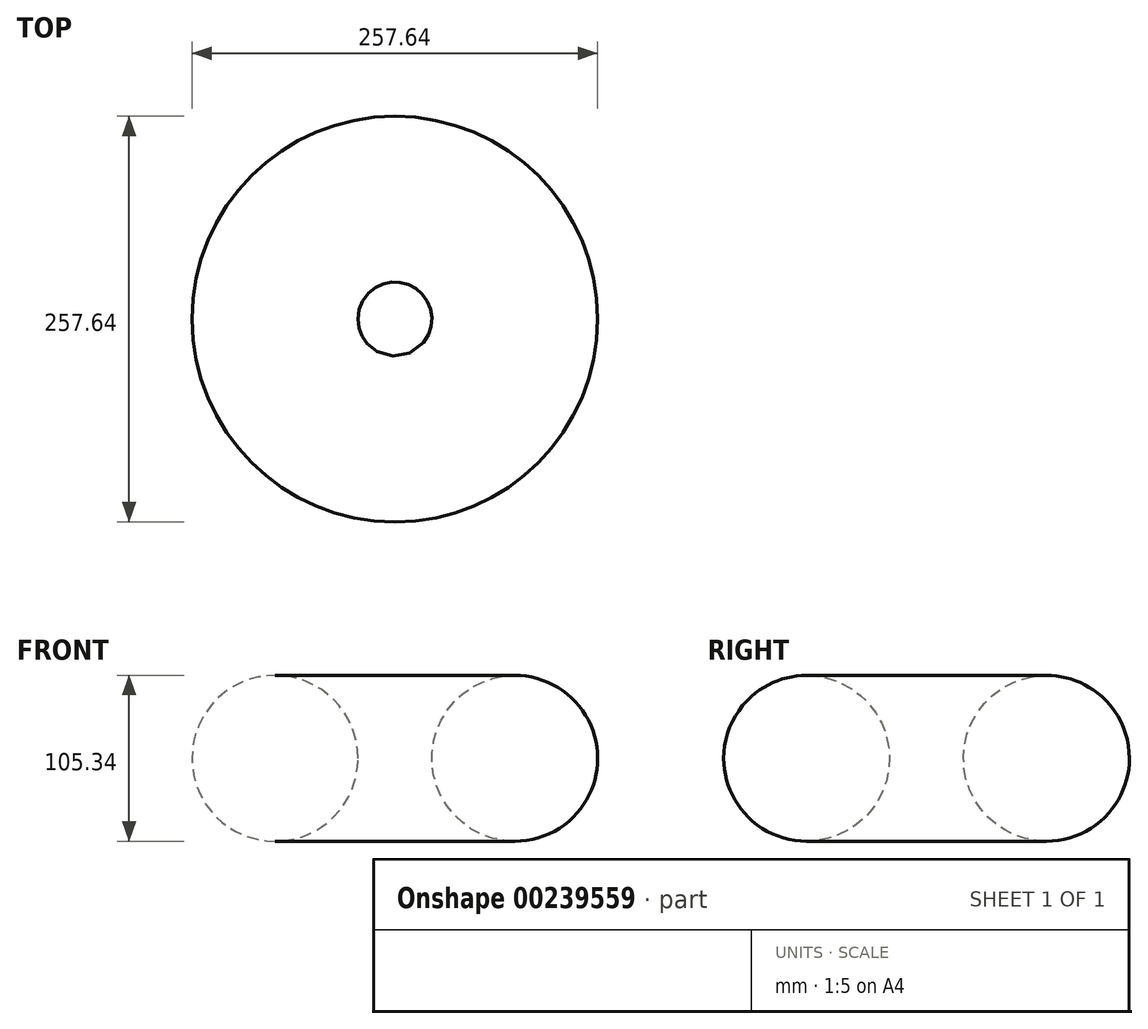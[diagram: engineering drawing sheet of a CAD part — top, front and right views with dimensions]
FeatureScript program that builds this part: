
annotation { "Feature Type Name" : "Feature", "Feature Type Description" : "" }
export const myFeature = defineFeature(function(context is Context, id is Id, definition is map)
    precondition{}
    {
        {
            var Q0;
            Q0=qCreatedBy(makeId("Front.planeOp"),FACE);
            var sketch = newSketch(context, id + "F0", { "sketchPlane" : qUnion([Q0])});
            skCircle(sketch, "E0", {"center": v(0, 0) * mm, "radius": 52.67 * mm});
            skLineSegment(sketch, "E1", {"start": v(-76.15, 76.3) * mm, "end": v(-76.15, -77.22) * mm, "construction": true});
            skSolve(sketch);
        }
        {
            var Q0;
            Q0=sQuery(id+"F0.wireOp",EDGE,"E0");
            var Q1;
            Q1=sQuery(id+"F0.wireOp",EDGE,"E1");
            revolve(context, id + "F1", {"bodyType" : ToolBodyType.SURFACE, "surfaceEntities" : qUnion([Q0]), "axis" : qUnion([Q1]), "revolveType" : RevolveType.FULL});
        }
    });
